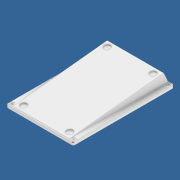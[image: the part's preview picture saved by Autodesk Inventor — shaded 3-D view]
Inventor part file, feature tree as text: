
AUTODESK INVENTOR PART (.ipt)
format: ipt  version: 2020 (Build 240168000, 168)  size: 340,480 bytes
history: native  units: in
note: dims shown in document units (in); Inventor stores cm internally (conversion verified against a paired STEP export)
features: extrude x12, sketch x12, fillet x3, plane x2, chamfer x1
ambient origin geometry x8: Origin, YZ Plane, XZ Plane, XY Plane, X Axis, Y Axis, Z Axis, Center Point
bodies: Solid1 (feature_tree)
feature tree (30):
  extrude  "Extrusion1"  Depth=3.7795in
  fillet  "Fillet1"  Radius=0.1181in
  extrude  "Extrusion2"  Depth=0.0787in
  extrude  "Extrusion4"  Depth=0.0787in
  extrude  "Extrusion5"  Depth=0.1063in
  extrude  "Extrusion8"  Depth=0.1063in
  extrude  "Extrusion17"  Depth=0.1063in
  extrude  "Extrusion19"  Depth=0.1063in
  extrude  "Extrusion21"  Depth=0.3937in TaperAngle=0.0deg
  extrude  "Extrusion24"  Depth=0.1772in
  plane  "Work Plane4"
  extrude  "Extrusion25"  Depth=3.7402in
  plane  "Work Plane5"
  extrude  "Extrusion27"  Depth=2.1181in
  fillet  "Fillet5"  Radius=2.1181in
  fillet  "Fillet7"  Radius=0.2402in
  extrude  "Extrusion28"  Depth=0.0787in
  sketch  "Sketch35"  dims[d62=0.2402in d63=0.2402in d64=0.2402in d65=0.1969in d66=0.1969in d67=0.1969in d68=0.1969in d69=0.1969in d70=0.1969in d71=0.1969in d72=0.1969in d73=0.0394in d74=0.0in d106=0.748in d107=1.3386in d108=0.0788in d109=0.6654in d110=0.7087in d111=0.0in d116=0.1354in d117=0.748in d118=0.0in d122=0.0394in d123=0.0in d137=0.1575in d138=0.1575in d139=0.1575in d141=0.1575in d142=0.0118in d143=0.0in d144=0.3937in d145=0.1575in d146=0.1969in d147=0.7874in d148=0.0in d157=0.6299in d158=0.3346in d159=0.7441in d160=0.1311in d161=0.3937in d162=0.0in d163=0.0787in d166=0.1669in d167=0.1181in d168=0.1181in d169=0.0394in d170=0.0in d171=0.0197in d172=0.0787in d173=45.0deg]
  chamfer  "Chamfer2"  Distance=0.2402in
  sketch  "Sketch1"  dims[d0=2.5118in d1=3.7795in d2=0.1181in d3=0.0in]
  sketch  "Sketch2"  dims[d4=0.0591in d5=0.0787in]
  sketch  "Sketch4"  dims[d6=0.0787in d7=0.0787in]
  sketch  "Sketch5"  dims[d8=0.0787in d9=0.1063in]
  sketch  "Sketch9"  dims[d10=0.1063in d11=0.1063in]
  sketch  "Sketch20"  dims[d12=0.1063in d13=0.1063in]
  sketch  "Sketch22"  dims[d14=0.1063in d15=0.1063in]
  sketch  "Sketch29"  dims[d16=0.1063in d17=0.3937in d18=0.0in]
  sketch  "Sketch31"  dims[d37=2.1181in d38=0.1772in]
  sketch  "Sketch33"  dims[d39=3.7402in d40=3.7402in]
  sketch  "Sketch34"  dims[d41=0.3752in d42=0.0in d44=1.1956in d45=2.1181in d46=0.0in d61=0.2402in]
